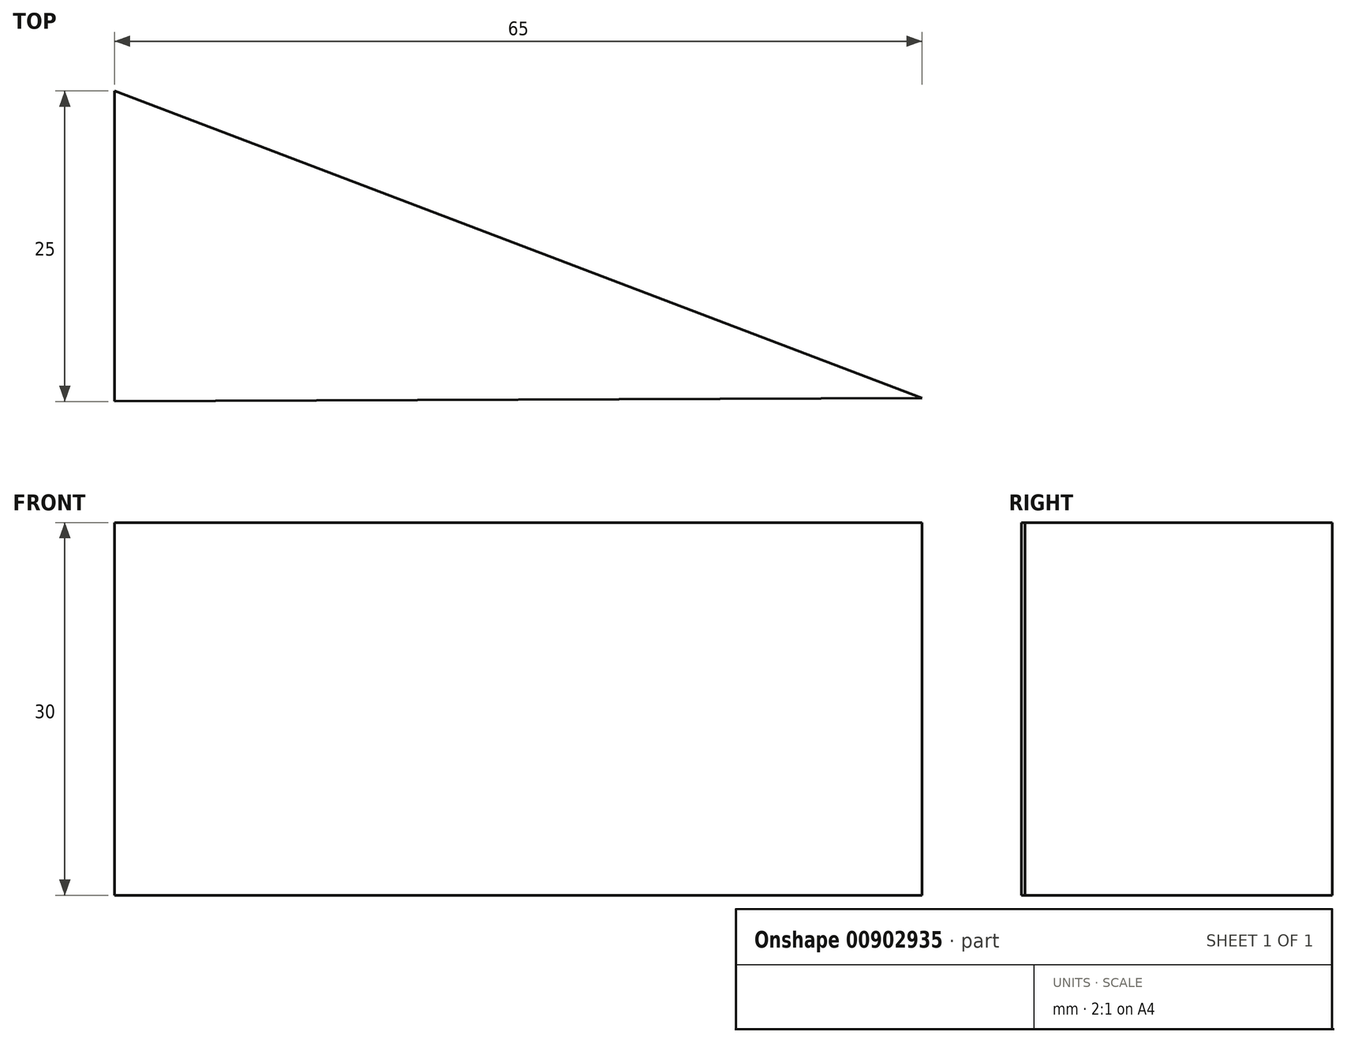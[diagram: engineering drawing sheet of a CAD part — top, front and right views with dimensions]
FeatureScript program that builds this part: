
annotation { "Feature Type Name" : "Feature", "Feature Type Description" : "" }
export const myFeature = defineFeature(function(context is Context, id is Id, definition is map)
    precondition{}
    {
        {
            var Q0;
            Q0=qCreatedBy(makeId("Top.planeOp"),FACE);
            var sketch = newSketch(context, id + "F0", { "sketchPlane" : qUnion([Q0])});
            skLineSegment(sketch, "E0", {"start": v(-19.78, 12.95) * mm, "end": v(-19.78, -12.05) * mm});
            skLineSegment(sketch, "E1", {"start": v(-19.78, -12.05) * mm, "end": v(45.22, -11.77) * mm});
            skLineSegment(sketch, "E2", {"start": v(45.22, -11.77) * mm, "end": v(-19.78, 12.95) * mm});
            skPoint(sketch, "E3.endSnap0", {"position": v(12.72, -11.9) * mm});
            skSolve(sketch);
        }
        {
            var Q0;
            Q0=makeQuery(id+"F0.imprint","IMPRINT",FACE,{"disambiguationData":[TD([[makeQuery(id+"F0.imprint","IMPRINT",EDGE,{"derivedFrom":sQuery(id+"F0.wireOp",EDGE,"E0")}),1.0]])]});
            extrude(context, id + "F1", {"entities" : qUnion([Q0]), "depth" : 30 * mm});
        }
    });
